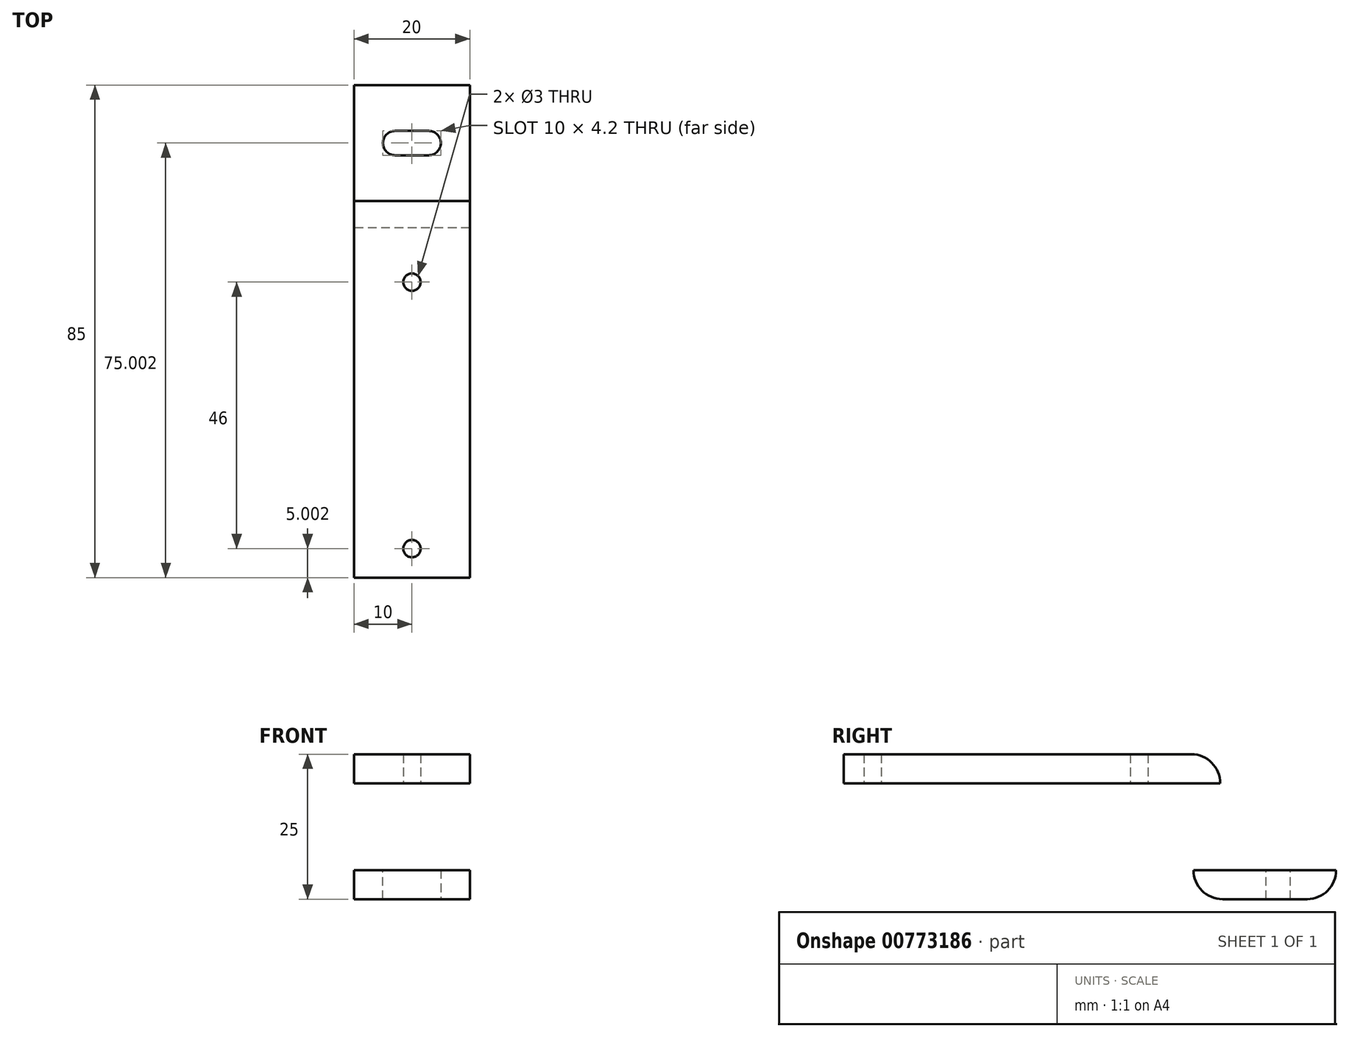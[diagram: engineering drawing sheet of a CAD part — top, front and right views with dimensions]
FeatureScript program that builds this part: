
annotation { "Feature Type Name" : "Feature", "Feature Type Description" : "" }
export const myFeature = defineFeature(function(context is Context, id is Id, definition is map)
    precondition{}
    {
        {
            var Q0;
            Q0=qCreatedBy(makeId("Right.planeOp"),FACE);
            var sketch = newSketch(context, id + "F0", { "sketchPlane" : qUnion([Q0])});
            skLineSegment(sketch, "E0.bottom", {"start": v(56.21, 5) * mm, "end": v(-8.79, 5) * mm});
            skLineSegment(sketch, "E0.top", {"start": v(56.21, 0) * mm, "end": v(-8.79, 0) * mm});
            skLineSegment(sketch, "E0.left", {"start": v(56.21, 5) * mm, "end": v(56.21, 0) * mm});
            skLineSegment(sketch, "E0.right", {"start": v(-8.79, 5) * mm, "end": v(-8.79, 0) * mm});
            skLineSegment(sketch, "E1.bottom", {"start": v(56.21, 0) * mm, "end": v(47.21, 0) * mm});
            skLineSegment(sketch, "E1.top", {"start": v(56.21, -15) * mm, "end": v(51.6, -15) * mm});
            skLineSegment(sketch, "E1.left", {"start": v(56.21, 0) * mm, "end": v(56.21, -15) * mm});
            skLineSegment(sketch, "E2.bottom", {"start": v(51.6, -15) * mm, "end": v(76.21, -15) * mm});
            skLineSegment(sketch, "E2.top", {"start": v(51.6, -20) * mm, "end": v(76.21, -20) * mm});
            skLineSegment(sketch, "E2.right", {"start": v(76.21, -15) * mm, "end": v(76.21, -20) * mm});
            skFitSpline(sketch, "E3", {"points": [v(47.21, 0) * mm, v(51.6, -15) * mm], "startDerivative": vector(5, -9.27) * mm, "endDerivative": vector(1.79, -10.97) * mm});
            skFitSpline(sketch, "E4", {"points": [v(51.6, -15) * mm, v(51.6, -20) * mm], "startDerivative": vector(0, -5) * mm, "endDerivative": vector(0, -5) * mm});
            skSolve(sketch);
        }
        {
            var Q0;
            Q0=makeQuery(id+"F0.imprint","IMPRINT",FACE,{"disambiguationData":[TD([[makeQuery(id+"F0.imprint","IMPRINT",EDGE,{"derivedFrom":sQuery(id+"F0.wireOp",EDGE,"E2.top")}),1.0]])]});
            var Q1;
            Q1=makeQuery(id+"F0.imprint","IMPRINT",FACE,{"disambiguationData":[TD([[makeQuery(id+"F0.imprint","IMPRINT",EDGE,{"derivedFrom":sQuery(id+"F0.wireOp",EDGE,"E1.bottom")}),1.0]])]});
            var Q2;
            Q2=makeQuery(id+"F0.imprint","IMPRINT",FACE,{"disambiguationData":[TD([[makeQuery(id+"F0.imprint","IMPRINT",EDGE,{"derivedFrom":sQuery(id+"F0.wireOp",EDGE,"E0.bottom")}),1.0]])]});
            extrude(context, id + "F1", {"entities" : qUnion([Q0, Q1, Q2]), "depth" : 20 * mm, "offsetDistance" : 25 * mm});
        }
        {
            var Q0;
            Q0=makeQuery(id+"F1.opExtrude","SWEPT_FACE",FACE,{"disambiguationData":[OSD([sQuery(id+"F0.wireOp",EDGE,"E0.top")])]});
            var sketch = newSketch(context, id + "F2", { "sketchPlane" : qUnion([Q0])});
            skCircle(sketch, "E5", {"center": v(10, -42.21) * mm, "radius": 1.5 * mm});
            skPoint(sketch, "E5.centerSnap0", {"position": v(10, -47.21) * mm});
            skCircle(sketch, "E6", {"center": v(10, 3.79) * mm, "radius": 1.5 * mm});
            skPoint(sketch, "E6.centerSnap0", {"position": v(10, 8.79) * mm});
            skSolve(sketch);
        }
        {
            var Q0;
            Q0=makeQuery(id+"F2.imprint","IMPRINT",FACE,{"disambiguationData":[TD([[makeQuery(id+"F2.imprint","IMPRINT",EDGE,{"derivedFrom":sQuery(id+"F2.wireOp",EDGE,"E5")}),1.0]])]});
            var Q1;
            Q1=makeQuery(id+"F2.imprint","IMPRINT",FACE,{"disambiguationData":[TD([[makeQuery(id+"F2.imprint","IMPRINT",EDGE,{"derivedFrom":sQuery(id+"F2.wireOp",EDGE,"E6")}),1.0]])]});
            var Q2;
            Q2=sQuery(id+"F2.wireOp",EDGE,"E5");
            var Q3;
            Q3=sQuery(id+"F2.wireOp",EDGE,"E6");
            extrude(context, id + "F3", {"entities" : qUnion([Q0, Q1]), "operationType" : NewBodyOperationType.REMOVE, "surfaceEntities" : qUnion([Q2, Q3]), "oppositeDirection" : true, "depth" : 5 * mm, "offsetDistance" : 25 * mm});
        }
        {
            var Q0;
            Q0=makeQuery(id+"F1.opExtrude","SWEPT_FACE",FACE,{"disambiguationData":[OSD([sQuery(id+"F0.wireOp",EDGE,"E2.bottom")])]});
            var sketch = newSketch(context, id + "F4", { "sketchPlane" : qUnion([Q0])});
            skLineSegment(sketch, "E7.bottom", {"start": v(5, 68.31) * mm, "end": v(15, 68.31) * mm});
            skLineSegment(sketch, "E7.top", {"start": v(5, 64.11) * mm, "end": v(15, 64.11) * mm});
            skLineSegment(sketch, "E7.left", {"start": v(5, 68.31) * mm, "end": v(5, 64.11) * mm});
            skLineSegment(sketch, "E7.right", {"start": v(15, 68.31) * mm, "end": v(15, 64.11) * mm});
            skPoint(sketch, "E7.middle", {"position": v(10, 66.21) * mm});
            skPoint(sketch, "E7.middle.positionSnap0", {"position": v(10, 76.21) * mm});
            skPoint(sketch, "E7.middle.positionSnap1", {"position": v(0, 66.21) * mm});
            skPoint(sketch, "E7.centerSnap0", {"position": v(10, 76.21) * mm});
            skPoint(sketch, "E7.centerSnap1", {"position": v(0, 66.21) * mm});
            skSolve(sketch);
        }
        {
            var Q0;
            Q0=makeQuery(id+"F4.imprint","IMPRINT",FACE,{"disambiguationData":[TD([[makeQuery(id+"F4.imprint","IMPRINT",EDGE,{"derivedFrom":sQuery(id+"F4.wireOp",EDGE,"E7.bottom")}),-1.0]])]});
            extrude(context, id + "F5", {"entities" : qUnion([Q0]), "operationType" : NewBodyOperationType.REMOVE, "oppositeDirection" : true, "depth" : 5 * mm, "offsetDistance" : 25 * mm});
        }
        {
            var Q0;
            Q0=makeQuery(id+"F5.boolean.opBoolean","COPY",EDGE,{"derivedFrom":makeQuery(id+"F5.opExtrude","SWEPT_EDGE",EDGE,{"disambiguationData":[OSD([sQuery(id+"F4.wireOp",EDGE,"E7.bottom"),sQuery(id+"F4.wireOp",EDGE,"E7.left")])]})});
            var Q1;
            Q1=makeQuery(id+"F5.boolean.opBoolean","COPY",EDGE,{"derivedFrom":makeQuery(id+"F5.opExtrude","SWEPT_EDGE",EDGE,{"disambiguationData":[OSD([sQuery(id+"F4.wireOp",EDGE,"E7.bottom"),sQuery(id+"F4.wireOp",EDGE,"E7.right")])]})});
            var Q2;
            Q2=makeQuery(id+"F5.boolean.opBoolean","COPY",EDGE,{"derivedFrom":makeQuery(id+"F5.opExtrude","SWEPT_EDGE",EDGE,{"disambiguationData":[OSD([sQuery(id+"F4.wireOp",EDGE,"E7.top"),sQuery(id+"F4.wireOp",EDGE,"E7.right")])]})});
            var Q3;
            Q3=makeQuery(id+"F5.boolean.opBoolean","COPY",EDGE,{"derivedFrom":makeQuery(id+"F5.opExtrude","SWEPT_EDGE",EDGE,{"disambiguationData":[OSD([sQuery(id+"F4.wireOp",EDGE,"E7.top"),sQuery(id+"F4.wireOp",EDGE,"E7.left")])]})});
            fillet(context, id + "F6", {"entities" : qUnion([Q0, Q1, Q2, Q3]), "radius" : 2.1 * mm, "tangentPropagation" : true, "allowEdgeOverflow" : false});
        }
        {
            var Q0;
            Q0=makeQuery(id+"F1.opExtrude","SWEPT_EDGE",EDGE,{"disambiguationData":[OSD([sQuery(id+"F0.wireOp",EDGE,"E0.bottom"),sQuery(id+"F0.wireOp",EDGE,"E0.left")])]});
            var Q1;
            Q1=makeQuery(id+"F1.opExtrude","SWEPT_EDGE",EDGE,{"disambiguationData":[OSD([sQuery(id+"F0.wireOp",EDGE,"E2.top"),sQuery(id+"F0.wireOp",EDGE,"E2.left")])]});
            fillet(context, id + "F7", {"entities" : qUnion([Q0, Q1]), "radius" : 5 * mm, "tangentPropagation" : true, "allowEdgeOverflow" : false});
        }
    });
